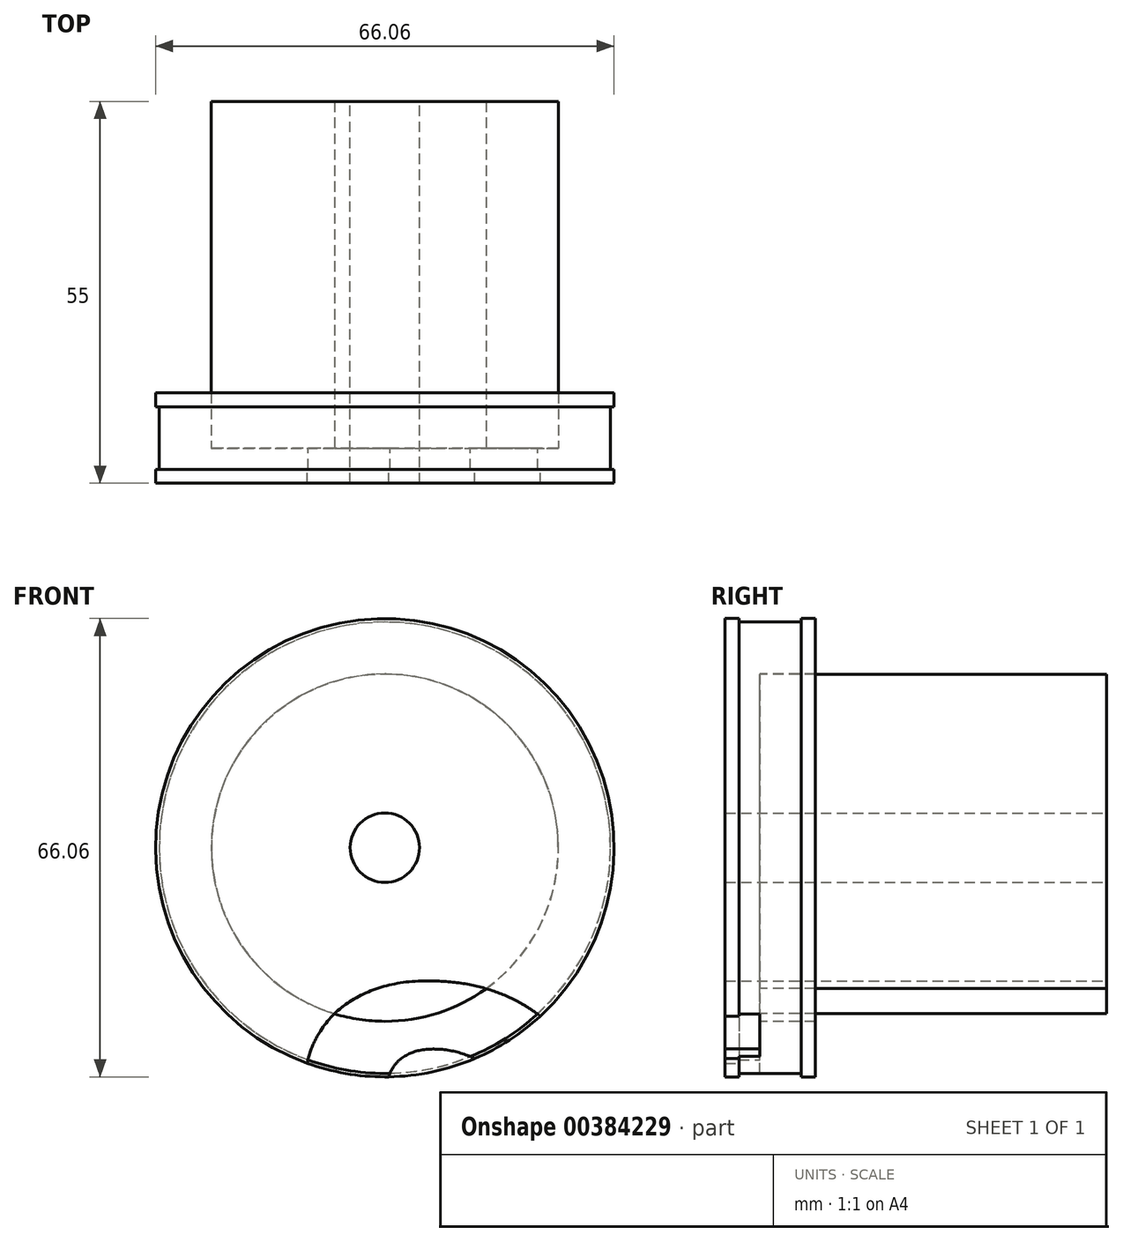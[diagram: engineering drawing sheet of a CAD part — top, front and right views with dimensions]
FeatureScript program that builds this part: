
annotation { "Feature Type Name" : "Feature", "Feature Type Description" : "" }
export const myFeature = defineFeature(function(context is Context, id is Id, definition is map)
    precondition{}
    {
        {
            var Q0;
            Q0=qCreatedBy(makeId("Top.planeOp"),FACE);
            var sketch = newSketch(context, id + "F0", { "sketchPlane" : qUnion([Q0])});
            skLineSegment(sketch, "E0", {"start": v(0.63, 0) * mm, "end": v(33.03, 0) * mm});
            skLineSegment(sketch, "E1", {"start": v(33.03, 0) * mm, "end": v(33.03, 2) * mm});
            skLineSegment(sketch, "E2", {"start": v(33.03, 2) * mm, "end": v(32.53, 2) * mm});
            skLineSegment(sketch, "E3", {"start": v(32.53, 2) * mm, "end": v(32.53, 11) * mm});
            skLineSegment(sketch, "E4", {"start": v(32.53, 11) * mm, "end": v(33.03, 11) * mm});
            skLineSegment(sketch, "E5", {"start": v(33.03, 11) * mm, "end": v(33.03, 13) * mm});
            skLineSegment(sketch, "E6", {"start": v(33.03, 13) * mm, "end": v(25.03, 13) * mm});
            skLineSegment(sketch, "E7", {"start": v(25.03, 13) * mm, "end": v(25.03, 5) * mm});
            skLineSegment(sketch, "E8", {"start": v(25.03, 5) * mm, "end": v(0, 5) * mm});
            skLineSegment(sketch, "E9", {"start": v(0, 5) * mm, "end": v(0, 0) * mm});
            skLineSegment(sketch, "E10", {"start": v(0, 0) * mm, "end": v(0.63, 0) * mm});
            skLineSegment(sketch, "E11", {"start": v(0, 5) * mm, "end": v(0, 15) * mm});
            skLineSegment(sketch, "E12", {"start": v(0, 15) * mm, "end": v(5, 15) * mm});
            skLineSegment(sketch, "E13", {"start": v(5, 15) * mm, "end": v(5, 5) * mm});
            skSolve(sketch);
        }
        {
            var Q0;
            {var subQ0=sQuery(id+"F0.wireOp",EDGE,"E11");Q0=makeQuery(id+"F0.imprint","IMPRINT",FACE,{"disambiguationData":[TD([[makeQuery(id+"F0.imprint","IMPRINT",EDGE,{"derivedFrom":subQ0}),-1.0]])]});}
            var Q1;
            Q1=makeQuery(id+"F0.imprint","IMPRINT",FACE,{"disambiguationData":[TD([[makeQuery(id+"F0.imprint","IMPRINT",EDGE,{"derivedFrom":sQuery(id+"F0.wireOp",EDGE,"E0")}),1.0]])]});
            var Q2;
            Q2=sQuery(id+"F0.wireOp",EDGE,"E11");
            revolve(context, id + "F1", {"entities" : qUnion([Q0, Q1]), "axis" : qUnion([Q2]), "revolveType" : RevolveType.FULL});
        }
        {
            var Q0;
            Q0=makeQuery(id+"F1.opRevolve","SWEPT_FACE",FACE,{"disambiguationData":[OSD([sQuery(id+"F0.wireOp",EDGE,"E12")])]});
            var sketch = newSketch(context, id + "F2", { "sketchPlane" : qUnion([Q0])});
            skCircle(sketch, "E14.0.0", {"center": v(0, 0) * mm, "radius": 5 * mm});
            skCircle(sketch, "E15", {"center": v(0, 0) * mm, "radius": 1.75 * mm});
            skSolve(sketch);
        }
        {
            var Q0;
            Q0=makeQuery(id+"F2.imprint","IMPRINT",FACE,{"disambiguationData":[TD([[makeQuery(id+"F2.imprint","IMPRINT",EDGE,{"derivedFrom":sQuery(id+"F2.wireOp",EDGE,"E15")}),1.0]])]});
            extrude(context, id + "F3", {"entities" : qUnion([Q0]), "operationType" : NewBodyOperationType.REMOVE, "oppositeDirection" : true, "depth" : 80 * mm});
        }
        {
            var Q0;
            Q0=makeQuery(id+"F1.opRevolve","SWEPT_FACE",FACE,{"disambiguationData":[OSD([sQuery(id+"F0.wireOp",EDGE,"E8")])]});
            var sketch = newSketch(context, id + "F4", { "sketchPlane" : qUnion([Q0])});
            skText(sketch, "E16", { "text": "SÚPER", "fontName": "OpenSans-Bold.ttf"});
            const initialGuessF4  = {"E16": [-0.12174, 0.03645, 1, 0, 0.05485]};
            skSetInitialGuess(sketch, initialGuessF4);
            skSolve(sketch);
        }
        {
            var Q0;
            Q0=qSketchRegion(id+"F4",true);
            extrude(context, id + "F5", {"entities" : qUnion([Q0]), "operationType" : NewBodyOperationType.REMOVE, "oppositeDirection" : true, "depth" : 25 * mm});
        }
        {
            var Q0;
            Q0=makeQuery(id+"F5.boolean.opBoolean","SPLIT",FACE,{"disambiguationData":[TD([makeQuery(id+"F1.opRevolve","SWEPT_FACE",FACE,{"disambiguationData":[OSD([sQuery(id+"F0.wireOp",EDGE,"E7")])]})])],"derivedFrom":makeQuery(id+"F1.opRevolve","SWEPT_FACE",FACE,{"disambiguationData":[OSD([sQuery(id+"F0.wireOp",EDGE,"E8")])]})});
            var sketch = newSketch(context, id + "F6", { "sketchPlane" : qUnion([Q0])});
            skText(sketch, "E17", { "text": "21\'", "fontName": "OpenSans-Bold.ttf"});
            const initialGuessF6  = {"E17": [-0.02899, -0.0757, 1, 0, 0.05619]};
            skSetInitialGuess(sketch, initialGuessF6);
            skSolve(sketch);
        }
        {
            var Q0;
            Q0=qSketchRegion(id+"F6",true);
            extrude(context, id + "F7", {"entities" : qUnion([Q0]), "operationType" : NewBodyOperationType.REMOVE, "oppositeDirection" : true, "depth" : 25 * mm});
        }
        {
            var Q0;
            Q0=makeQuery(id+"F2.imprint","IMPRINT",FACE,{"disambiguationData":[TD([[makeQuery(id+"F2.imprint","IMPRINT",EDGE,{"derivedFrom":sQuery(id+"F2.wireOp",EDGE,"E14.0.0")}),-1.0]])]});
            var sketch = newSketch(context, id + "F8", { "sketchPlane" : qUnion([Q0])});
            skSolve(sketch);
        }
        {
            var Q0;
            Q0=qSketchRegion(id+"F8",true);
            var Q1;
            Q1=makeQuery(id+"F2.imprint","IMPRINT",FACE,{"disambiguationData":[TD([[makeQuery(id+"F2.imprint","IMPRINT",EDGE,{"derivedFrom":sQuery(id+"F2.wireOp",EDGE,"E15")}),1.0]])]});
            var Q2;
            Q2=makeQuery(id+"F2.imprint","IMPRINT",FACE,{"disambiguationData":[TD([[makeQuery(id+"F2.imprint","IMPRINT",EDGE,{"derivedFrom":sQuery(id+"F2.wireOp",EDGE,"E14.0.0")}),-1.0]])]});
            extrude(context, id + "F9", {"entities" : qUnion([Q0, Q1, Q2]), "operationType" : NewBodyOperationType.REMOVE, "oppositeDirection" : true, "depth" : 25 * mm});
        }
        {
            var Q0;
            Q0=makeQuery(id+"F5.boolean.opBoolean","SPLIT",FACE,{"disambiguationData":[TD([makeQuery(id+"F1.opRevolve","SWEPT_FACE",FACE,{"disambiguationData":[OSD([sQuery(id+"F0.wireOp",EDGE,"E7")])]})])],"derivedFrom":makeQuery(id+"F1.opRevolve","SWEPT_FACE",FACE,{"disambiguationData":[OSD([sQuery(id+"F0.wireOp",EDGE,"E8")])]})});
            var sketch = newSketch(context, id + "F10", { "sketchPlane" : qUnion([Q0])});
            skCircle(sketch, "E18.0.0", {"center": v(0, 0) * mm, "radius": 154.13 * mm});
            skCircle(sketch, "E19.0", {"center": v(0, 0) * mm, "radius": 5 * mm});
            skCircle(sketch, "E20", {"center": v(0, 0) * mm, "radius": 25 * mm});
            skSolve(sketch);
        }
        {
            var Q0;
            Q0=makeQuery(id+"F10.imprint","IMPRINT",FACE,{"disambiguationData":[TD([[makeQuery(id+"F10.imprint","IMPRINT",EDGE,{"derivedFrom":sQuery(id+"F10.wireOp",EDGE,"E19.0")}),1.0]])]});
            extrude(context, id + "F11", {"entities" : qUnion([Q0]), "operationType" : NewBodyOperationType.ADD, "depth" : 50 * mm});
        }
    });
